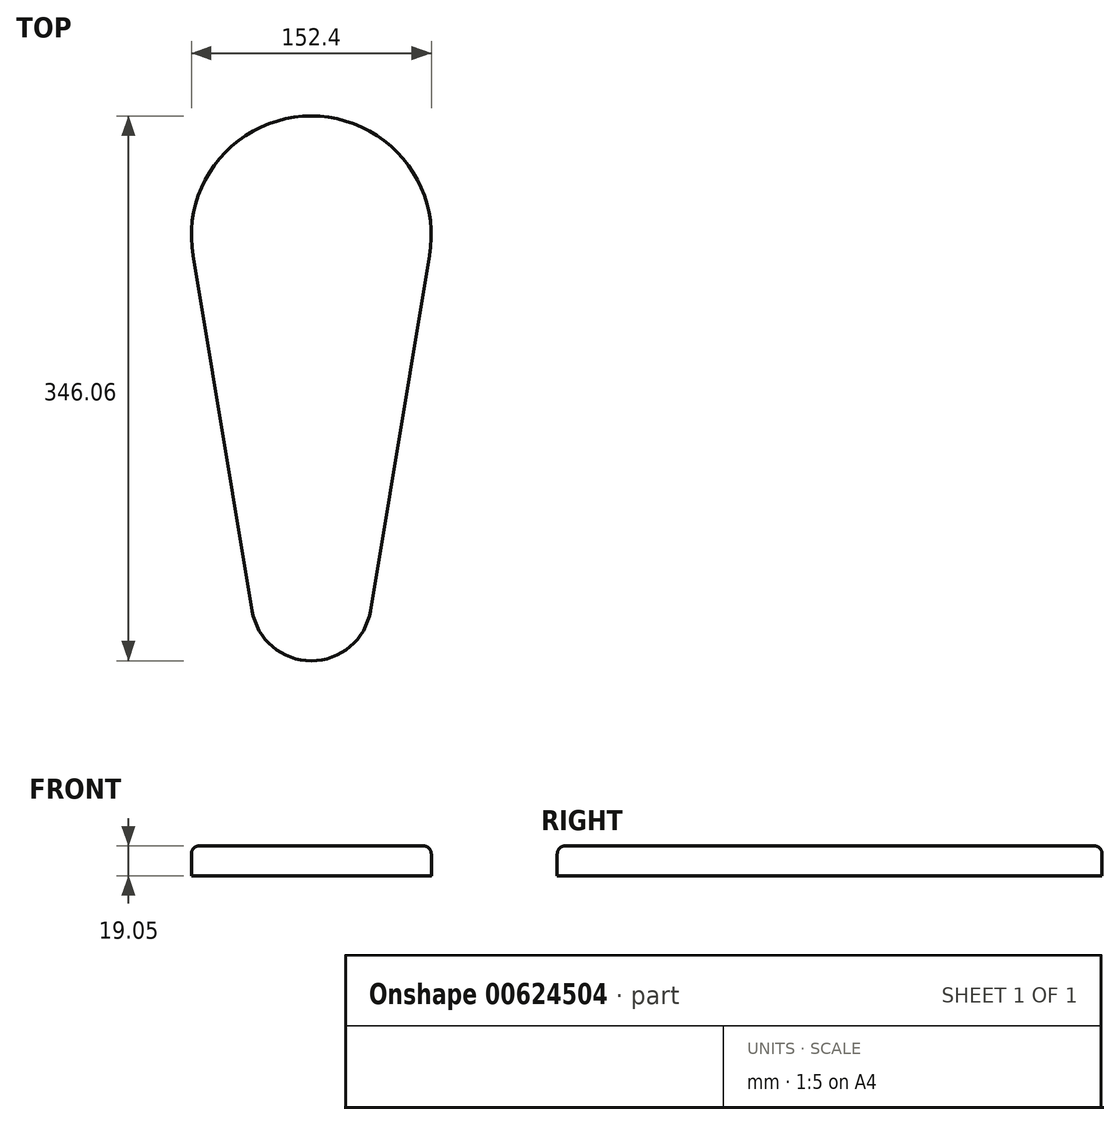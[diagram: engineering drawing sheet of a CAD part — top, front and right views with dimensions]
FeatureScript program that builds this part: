
annotation { "Feature Type Name" : "Feature", "Feature Type Description" : "" }
export const myFeature = defineFeature(function(context is Context, id is Id, definition is map)
    precondition{}
    {
        {
            var Q0;
            Q0=qCreatedBy(makeId("Top.planeOp"),FACE);
            var sketch = newSketch(context, id + "F0", { "sketchPlane" : qUnion([Q0])});
            skLineSegment(sketch, "E0", {"start": v(0, 0) * mm, "end": v(-37.58, 225.49) * mm});
            skArc(sketch, "E1", {"start": v(-37.58, 225.49) * mm, "mid": v(37.58, 314.22) * mm, "end": v(112.74, 225.49) * mm});
            skLineSegment(sketch, "E2", {"start": v(112.74, 225.49) * mm, "end": v(75.16, 0) * mm});
            skArc(sketch, "E3", {"start": v(0, 0) * mm, "mid": v(37.58, -31.84) * mm, "end": v(75.16, 0) * mm});
            skSolve(sketch);
        }
        {
            var Q0;
            Q0=makeQuery(id+"F0.imprint","IMPRINT",FACE,{"disambiguationData":[TD([[makeQuery(id+"F0.imprint","IMPRINT",EDGE,{"derivedFrom":sQuery(id+"F0.wireOp",EDGE,"E0")}),-1.0]])]});
            extrude(context, id + "F1", {"entities" : qUnion([Q0]), "depth" : 19.05 * mm, "offsetDistance" : 25.4 * mm});
        }
        {
            var Q0;
            Q0=makeQuery(id+"F1.opExtrude","CAP_FACE",FACE,{"disambiguationData":[OSD([sQuery(id+"F0.wireOp",EDGE,"E0"),sQuery(id+"F0.wireOp",EDGE,"E1"),sQuery(id+"F0.wireOp",EDGE,"E2"),sQuery(id+"F0.wireOp",EDGE,"E3")])],"isStart":false});
            fillet(context, id + "F2", {"entities" : qUnion([Q0]), "radius" : 5.08 * mm, "tangentPropagation" : true, "allowEdgeOverflow" : false});
        }
    });
